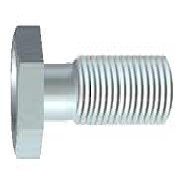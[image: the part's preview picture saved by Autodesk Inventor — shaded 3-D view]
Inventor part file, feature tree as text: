
AUTODESK INVENTOR PART (.ipt)
format: ipt  version: 2016 SP1 (Build 200210100, 210)  size: 178,176 bytes
history: native  units: mm (DEFAULTED — no unit token found)
features: sketch x4, extrude x2, chamfer x1, plane x1
ambient origin geometry x7: Origin, YZ Plane, XZ Plane, X Axis, Y Axis, Z Axis, Center Point
bodies: Solid1 (feature_tree), Body (feature_tree)
feature tree (8):
  extrude  "Head"  TaperAngle=90.0deg  [1 undecoded]
  extrude  "Indent"  TaperAngle=0.0deg  [1 undecoded]
  chamfer  "Chamfer1"  Distance=0.39751mm
  plane  "Work Plane1"
  sketch  "Sketch1"  dims[d1=4.1656mm d12=90.0deg]
  sketch  "Sketch2"  dims[d2=2.794mm d3=0.0mm]
  sketch  "Sketch4"  dims[d21=90.0deg d5=0.39751mm d6=0.39761mm d7=0.0mm d8=7.9248mm d9=26.9875mm d10=0.0mm d13=31.75mm d17=7.9248mm d18=6.33984mm d19=0.2804mm d20=0.0mm d77=45.0deg d80=0.0mm d81=0.0mm]
  sketch  "Sketch3"  dims[d4=30.0deg]
note: 2 required parameter values undecoded (feature->parameter linkage not recoverable at this tier; creation-order binding heuristic only, values carry confidence <= 0.55)
